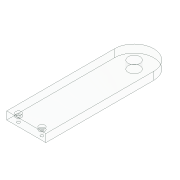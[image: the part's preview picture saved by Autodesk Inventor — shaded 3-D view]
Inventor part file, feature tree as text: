
AUTODESK INVENTOR PART (.ipt)
format: ipt  version: 2022.5 (Build 265521000, 521)  size: 112,640 bytes
history: native  units: mm
features: extrude x3, sketch x2, fillet x1, mirror x1
ambient origin geometry x8: Origin, YZ Plane, XZ Plane, XY Plane, X Axis, Y Axis, Z Axis, Center Point
bodies: Solid1 (feature_tree)
feature tree (7):
  extrude  "Extrusion1"  Depth=40.0mm
  fillet  "Fillet1"  Radius=8.0mm
  extrude  "Extrusion2"  Depth=20.0mm
  extrude  "Extrusion3"  Depth=8.0mm
  mirror  "Mirror1"
  sketch  "Sketch2"  dims[d0=12.0mm d1=40.0mm d2=8.0mm d3=0.0mm]
  sketch  "Sketch3"  dims[d5=110.0mm d6=20.0mm d7=8.0mm d8=3.0mm d9=0.0mm d10=0.0mm d11=6.0mm d12=2.5mm d13=0.0mm d14=12.0mm]
